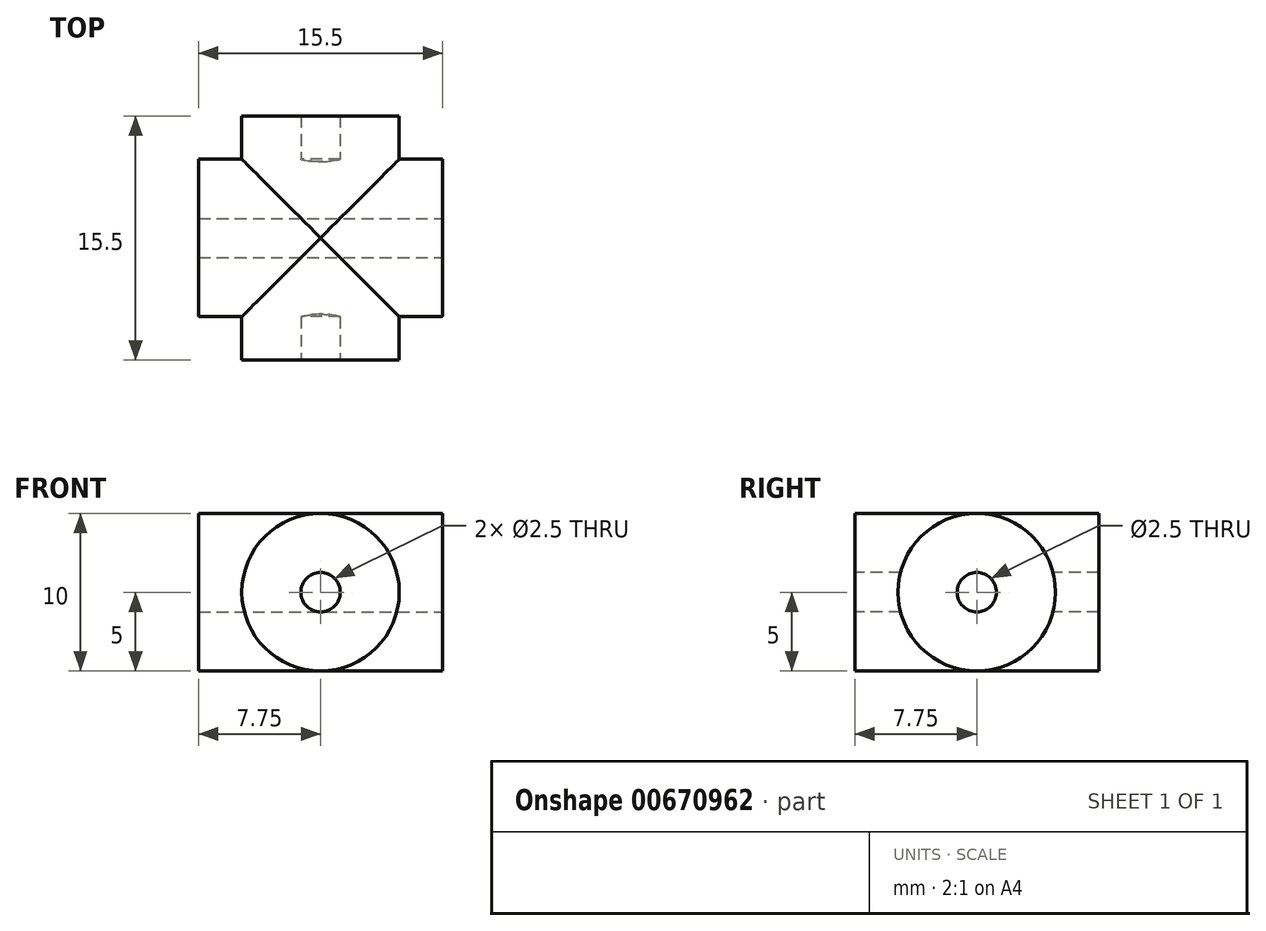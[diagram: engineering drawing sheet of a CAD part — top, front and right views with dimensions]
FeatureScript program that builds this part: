
annotation { "Feature Type Name" : "Feature", "Feature Type Description" : "" }
export const myFeature = defineFeature(function(context is Context, id is Id, definition is map)
    precondition{}
    {
        {
            var Q0;
            Q0=qCreatedBy(makeId("Front.planeOp"),FACE);
            var sketch = newSketch(context, id + "F0", { "sketchPlane" : qUnion([Q0])});
            skCircle(sketch, "E0", {"center": v(0, 0) * mm, "radius": 5 * mm});
            skSolve(sketch);
        }
        {
            var Q0;
            Q0 = qSketchRegion(id + "F0", true);
            extrude(context, id + "F1", {"entities" : qUnion([Q0]), "endBound" : BoundingType.SYMMETRIC, "depth" : 15.5 * mm, "offsetDistance" : 25 * mm});
        }
        {
            var Q0;
            Q0=makeQuery(id+"F1.opExtrude","CAP_FACE",FACE,{"disambiguationData":[OSD([sQuery(id+"F0.wireOp",EDGE,"E0")])],"isStart":false});
            var sketch = newSketch(context, id + "F2", { "sketchPlane" : qUnion([Q0])});
            skCircle(sketch, "E1", {"center": v(0, 0) * mm, "radius": 1.25 * mm});
            skSolve(sketch);
        }
        {
            var Q0;
            Q0 = qSketchRegion(id + "F2", true);
            extrude(context, id + "F3", {"entities" : qUnion([Q0]), "operationType" : NewBodyOperationType.REMOVE, "oppositeDirection" : true, "depth" : 25 * mm, "offsetDistance" : 25 * mm});
        }
        {
            var Q0;
            Q0=qCreatedBy(makeId("Right.planeOp"),FACE);
            var sketch = newSketch(context, id + "F4", { "sketchPlane" : qUnion([Q0])});
            skCircle(sketch, "E2", {"center": v(0, 0) * mm, "radius": 5 * mm});
            skSolve(sketch);
        }
        {
            var Q0;
            Q0 = qSketchRegion(id + "F4", true);
            extrude(context, id + "F5", {"entities" : qUnion([Q0]), "operationType" : NewBodyOperationType.ADD, "endBound" : BoundingType.SYMMETRIC, "depth" : 15.5 * mm, "offsetDistance" : 25 * mm});
        }
        {
            var Q0;
            Q0=makeQuery(id+"F5.opExtrude","CAP_FACE",FACE,{"disambiguationData":[OSD([sQuery(id+"F4.wireOp",EDGE,"E2")])],"isStart":false});
            var sketch = newSketch(context, id + "F6", { "sketchPlane" : qUnion([Q0])});
            skCircle(sketch, "E3", {"center": v(0, 0) * mm, "radius": 1.25 * mm});
            skSolve(sketch);
        }
        {
            var Q0;
            Q0 = qSketchRegion(id + "F6", true);
            extrude(context, id + "F7", {"entities" : qUnion([Q0]), "operationType" : NewBodyOperationType.REMOVE, "oppositeDirection" : true, "depth" : 25 * mm, "offsetDistance" : 25 * mm});
        }
    });
